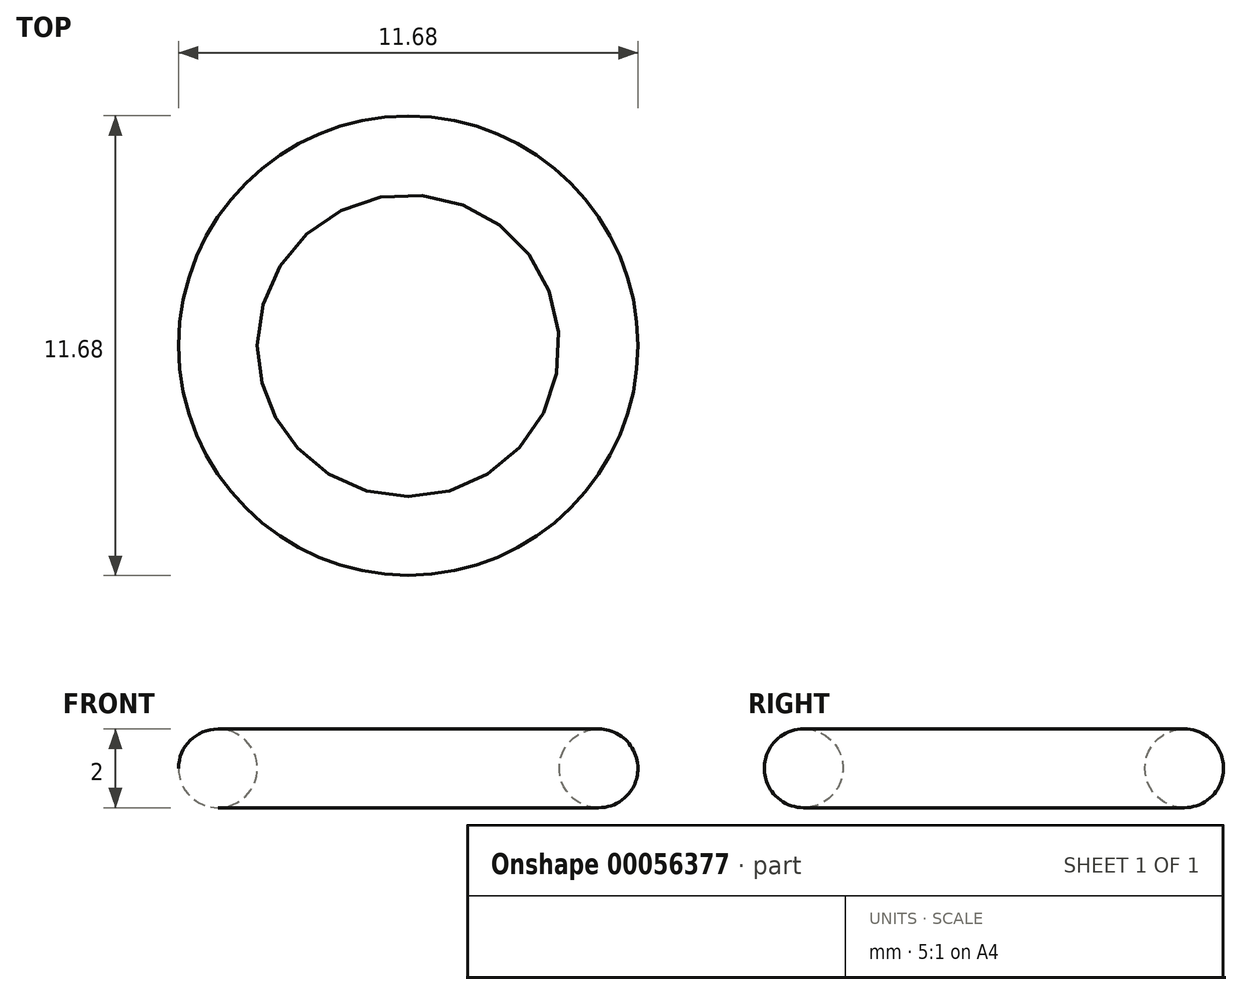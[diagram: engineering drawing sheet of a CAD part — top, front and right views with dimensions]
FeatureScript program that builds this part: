
annotation { "Feature Type Name" : "Feature", "Feature Type Description" : "" }
export const myFeature = defineFeature(function(context is Context, id is Id, definition is map)
    precondition{}
    {
        {
            var Q0;
            Q0=qCreatedBy(makeId("Front.planeOp"),FACE);
            var sketch = newSketch(context, id + "F0", { "sketchPlane" : qUnion([Q0])});
            skLineSegment(sketch, "E0", {"start": v(0, 0) * mm, "end": v(4.83, 0) * mm, "construction": true});
            skLineSegment(sketch, "E1", {"start": v(0, 0) * mm, "end": v(0, 4) * mm, "construction": true});
            skCircle(sketch, "E2", {"center": v(4.83, 0) * mm, "radius": 1 * mm});
            skSolve(sketch);
        }
        {
            var Q0;
            Q0=makeQuery(id+"F0.imprint","IMPRINT",FACE,{"disambiguationData":[TD([[makeQuery(id+"F0.imprint","IMPRINT",EDGE,{"derivedFrom":sQuery(id+"F0.wireOp",EDGE,"E2")}),1.0]])]});
            var Q1;
            Q1=sQuery(id+"F0.wireOp",EDGE,"E1");
            revolve(context, id + "F1", {"entities" : qUnion([Q0]), "axis" : qUnion([Q1]), "revolveType" : RevolveType.FULL});
        }
    });
